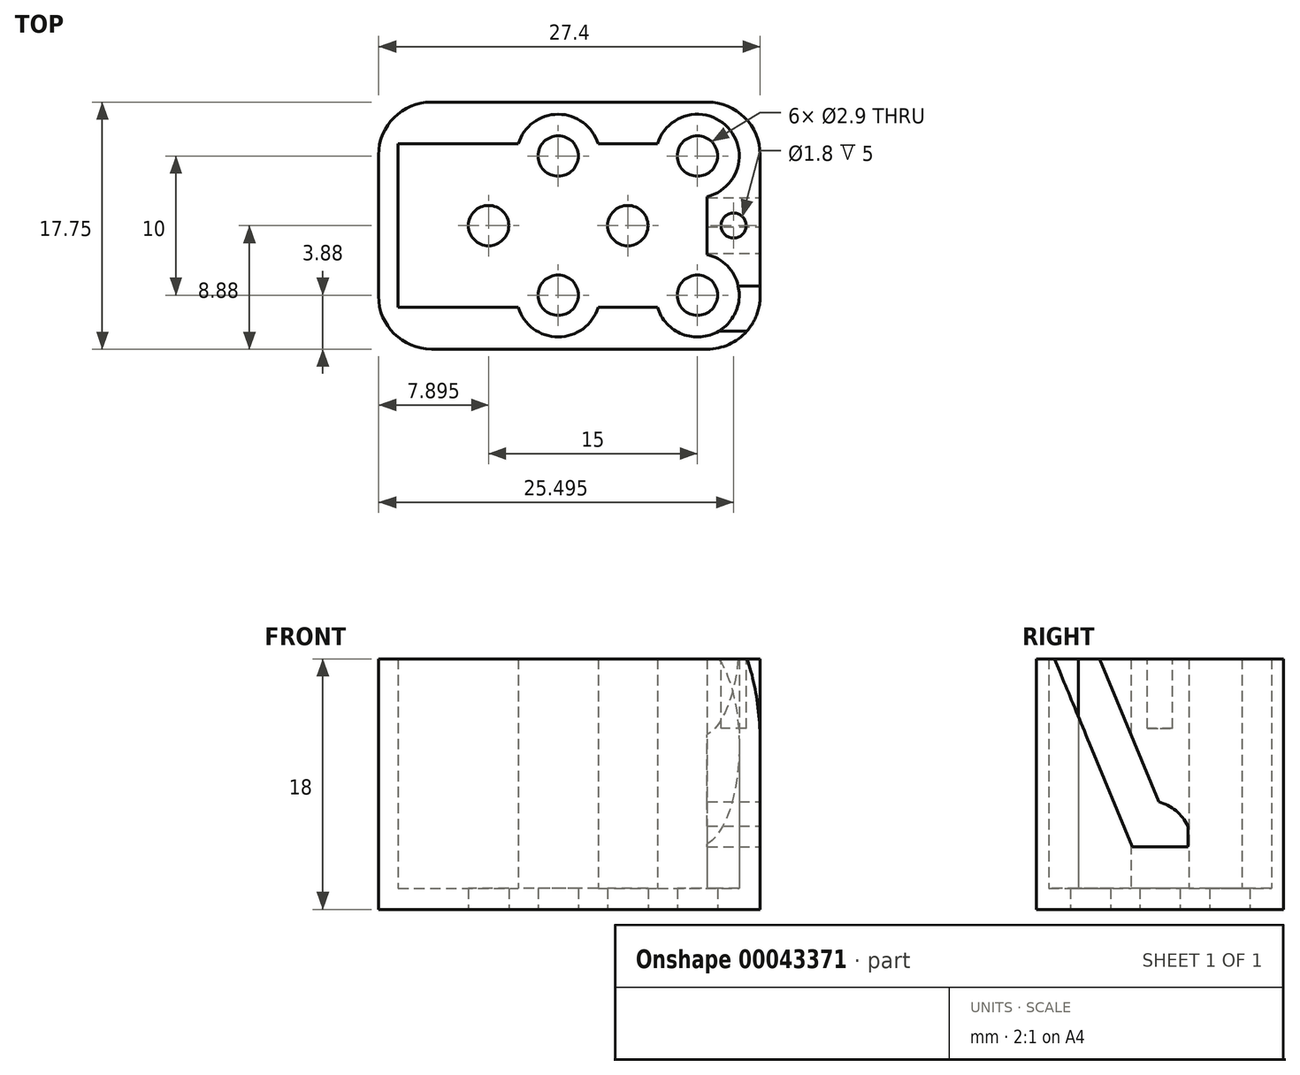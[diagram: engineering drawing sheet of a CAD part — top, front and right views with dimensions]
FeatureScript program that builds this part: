
annotation { "Feature Type Name" : "Feature", "Feature Type Description" : "" }
export const myFeature = defineFeature(function(context is Context, id is Id, definition is map)
    precondition{}
    {
        {
            var Q0;
            Q0=qCreatedBy(makeId("Top.planeOp"),FACE);
            var sketch = newSketch(context, id + "F0", { "sketchPlane" : qUnion([Q0])});
            skLineSegment(sketch, "E0.bottom", {"start": v(-11.23, 5.28) * mm, "end": v(10.27, 5.28) * mm});
            skLineSegment(sketch, "E0.top", {"start": v(-11.23, -6.47) * mm, "end": v(10.27, -6.47) * mm});
            skLineSegment(sketch, "E0.left", {"start": v(-11.23, 5.28) * mm, "end": v(-11.23, -6.47) * mm});
            skLineSegment(sketch, "E0.right", {"start": v(10.27, 5.28) * mm, "end": v(10.27, -6.47) * mm});
            skPoint(sketch, "E1", {"position": v(-0.48, -0.6) * mm});
            skPoint(sketch, "E1.positionSnap0", {"position": v(10.27, -0.6) * mm});
            skPoint(sketch, "E1.positionSnap1", {"position": v(-0.48, 5.28) * mm});
            skLineSegment(sketch, "E2.bottom", {"start": v(-12.63, 8.28) * mm, "end": v(11.67, 8.28) * mm});
            skLineSegment(sketch, "E2.left", {"start": v(-12.63, 8.28) * mm, "end": v(-12.63, -9.47) * mm});
            skPoint(sketch, "E3", {"position": v(-0.48, 8.28) * mm});
            skLineSegment(sketch, "E4.bottom", {"start": v(11.67, 8.28) * mm, "end": v(14.77, 8.28) * mm});
            skLineSegment(sketch, "E4.top", {"start": v(-12.63, -9.47) * mm, "end": v(14.77, -9.47) * mm});
            skLineSegment(sketch, "E4.right", {"start": v(14.77, 8.28) * mm, "end": v(14.77, -9.47) * mm});
            skPoint(sketch, "E5", {"position": v(5.27, -0.6) * mm});
            skCircle(sketch, "E6", {"center": v(5.27, -0.6) * mm, "radius": 1.45 * mm});
            skLineSegment(sketch, "E7.bottom", {"start": v(0.27, 4.4) * mm, "end": v(5.27, 4.4) * mm, "construction": true});
            skLineSegment(sketch, "E7.top", {"start": v(0.27, -5.6) * mm, "end": v(10.27, -5.6) * mm, "construction": true});
            skLineSegment(sketch, "E7.left", {"start": v(0.27, 4.4) * mm, "end": v(0.27, -5.6) * mm, "construction": true});
            skLineSegment(sketch, "E7.right", {"start": v(10.27, 4.4) * mm, "end": v(10.27, -5.6) * mm, "construction": true});
            skPoint(sketch, "E8.positionSnap1", {"position": v(5.27, 4.4) * mm});
            skCircle(sketch, "E9", {"center": v(10.27, 4.4) * mm, "radius": 1.45 * mm});
            skCircle(sketch, "E10.0.1.0", {"center": v(10.27, -5.6) * mm, "radius": 1.45 * mm});
            skCircle(sketch, "E10.1.0.0", {"center": v(0.27, 4.4) * mm, "radius": 1.45 * mm});
            skCircle(sketch, "E10.1.1.0", {"center": v(0.27, -5.6) * mm, "radius": 1.45 * mm});
            skLineSegment(sketch, "E10.direction1", {"start": v(10.27, 4.4) * mm, "end": v(7.27, 4.4) * mm, "construction": true});
            skCircle(sketch, "E11.1.0.0", {"center": v(-4.73, -0.6) * mm, "radius": 1.45 * mm});
            skLineSegment(sketch, "E11.direction1", {"start": v(5.27, -0.6) * mm, "end": v(-4.73, -0.6) * mm, "construction": true});
            skCircle(sketch, "E12", {"center": v(10.27, 4.4) * mm, "radius": 3 * mm});
            skCircle(sketch, "E13.0.1.0", {"center": v(10.27, -5.6) * mm, "radius": 3 * mm});
            skCircle(sketch, "E13.1.0.0", {"center": v(0.27, 4.4) * mm, "radius": 3 * mm});
            skCircle(sketch, "E13.1.1.0", {"center": v(0.27, -5.6) * mm, "radius": 3 * mm});
            skLineSegment(sketch, "E13.direction1", {"start": v(10.27, 4.4) * mm, "end": v(0.27, 4.4) * mm, "construction": true});
            skLineSegment(sketch, "E14.trimOffspring", {"start": v(3.27, 4.4) * mm, "end": v(0.27, 4.4) * mm, "construction": true});
            skLineSegment(sketch, "E15.trimOffspring", {"start": v(7.27, 4.4) * mm, "end": v(10.27, 4.4) * mm, "construction": true});
            skLineSegment(sketch, "E16", {"start": v(10.97, 1.5) * mm, "end": v(10.97, -2.67) * mm});
            skSolve(sketch);
        }
        {
            var Q0;
            {var subQ6=sQuery(id+"F0.wireOp",EDGE,"E0.left");Q0=makeQuery(id+"F0.imprint","IMPRINT",FACE,{"disambiguationData":[TD([[makeQuery(id+"F0.imprint","IMPRINT",EDGE,{"derivedFrom":subQ6}),1.0]])]});}
            var Q1;
            {var subQ0=sQuery(id+"F0.wireOp",EDGE,"E13.0.1.0");var subQ3=sQuery(id+"F0.wireOp",EDGE,"E0.top");var subQ4=makeQuery(id+"F0.imprint","INTERSECT",VERTEX,{"derivedFrom":[subQ3,subQ0]});Q1=makeQuery(id+"F0.imprint","IMPRINT",FACE,{"disambiguationData":[TD([[makeQuery(id+"F0.imprint","IMPRINT",EDGE,{"disambiguationData":[TD([[subQ4,-1.0]])],"derivedFrom":subQ3}),1.0]])]});}
            var Q2;
            {var subQ3=sQuery(id+"F0.wireOp",EDGE,"E0.bottom");var subQ5=sQuery(id+"F0.wireOp",EDGE,"E12");var subQ7=makeQuery(id+"F0.imprint","INTERSECT",VERTEX,{"derivedFrom":[subQ3,subQ5]});Q2=makeQuery(id+"F0.imprint","IMPRINT",FACE,{"disambiguationData":[TD([[makeQuery(id+"F0.imprint","IMPRINT",EDGE,{"disambiguationData":[TD([[subQ7,-1.0]])],"derivedFrom":subQ3}),-1.0]])]});}
            var Q3;
            {var subQ0=sQuery(id+"F0.wireOp",EDGE,"E13.0.1.0");var subQ3=sQuery(id+"F0.wireOp",EDGE,"E0.top");var subQ4=makeQuery(id+"F0.imprint","INTERSECT",VERTEX,{"derivedFrom":[subQ3,subQ0]});Q3=makeQuery(id+"F0.imprint","IMPRINT",FACE,{"disambiguationData":[TD([[makeQuery(id+"F0.imprint","IMPRINT",EDGE,{"disambiguationData":[TD([[subQ4,-1.0]])],"derivedFrom":subQ3}),-1.0]])]});}
            var Q4;
            {var subQ1=sQuery(id+"F0.wireOp",EDGE,"E0.bottom");var subQ4=sQuery(id+"F0.wireOp",EDGE,"E13.1.0.0");var subQ6=makeQuery(id+"F0.imprint","INTERSECT",VERTEX,{"disambiguationData":[OD(0.0)],"derivedFrom":[subQ1,subQ4]});Q4=makeQuery(id+"F0.imprint","IMPRINT",FACE,{"disambiguationData":[TD([[makeQuery(id+"F0.imprint","IMPRINT",EDGE,{"disambiguationData":[TD([[subQ6,-1.0]])],"derivedFrom":subQ1}),1.0]])]});}
            var Q5;
            {var subQ0=sQuery(id+"F0.wireOp",EDGE,"E13.1.0.0");var subQ1=sQuery(id+"F0.wireOp",EDGE,"E0.bottom");var subQ3=makeQuery(id+"F0.imprint","INTERSECT",VERTEX,{"disambiguationData":[OD(0.0)],"derivedFrom":[subQ1,subQ0]});Q5=makeQuery(id+"F0.imprint","IMPRINT",FACE,{"disambiguationData":[TD([[makeQuery(id+"F0.imprint","IMPRINT",EDGE,{"disambiguationData":[TD([[subQ3,-1.0]])],"derivedFrom":subQ1}),-1.0]])]});}
            var Q6;
            {var subQ3=sQuery(id+"F0.wireOp",EDGE,"E0.bottom");var subQ5=sQuery(id+"F0.wireOp",EDGE,"E12");var subQ7=makeQuery(id+"F0.imprint","INTERSECT",VERTEX,{"derivedFrom":[subQ3,subQ5]});Q6=makeQuery(id+"F0.imprint","IMPRINT",FACE,{"disambiguationData":[TD([[makeQuery(id+"F0.imprint","IMPRINT",EDGE,{"disambiguationData":[TD([[subQ7,-1.0]])],"derivedFrom":subQ3}),1.0]])]});}
            var Q7;
            {var subQ0=sQuery(id+"F0.wireOp",EDGE,"E13.1.1.0");var subQ1=sQuery(id+"F0.wireOp",EDGE,"E0.top");var subQ3=makeQuery(id+"F0.imprint","INTERSECT",VERTEX,{"disambiguationData":[OD(0.0)],"derivedFrom":[subQ1,subQ0]});Q7=makeQuery(id+"F0.imprint","IMPRINT",FACE,{"disambiguationData":[TD([[makeQuery(id+"F0.imprint","IMPRINT",EDGE,{"disambiguationData":[TD([[subQ3,-1.0]])],"derivedFrom":subQ1}),1.0]])]});}
            var Q8;
            {var subQ1=sQuery(id+"F0.wireOp",EDGE,"E0.top");var subQ4=sQuery(id+"F0.wireOp",EDGE,"E13.1.1.0");var subQ6=makeQuery(id+"F0.imprint","INTERSECT",VERTEX,{"disambiguationData":[OD(0.0)],"derivedFrom":[subQ1,subQ4]});Q8=makeQuery(id+"F0.imprint","IMPRINT",FACE,{"disambiguationData":[TD([[makeQuery(id+"F0.imprint","IMPRINT",EDGE,{"disambiguationData":[TD([[subQ6,-1.0]])],"derivedFrom":subQ1}),-1.0]])]});}
            var Q9;
            {var subQ0=sQuery(id+"F0.wireOp",EDGE,"E16");Q9=makeQuery(id+"F0.imprint","IMPRINT",FACE,{"disambiguationData":[TD([[makeQuery(id+"F0.imprint","IMPRINT",EDGE,{"derivedFrom":subQ0}),-1.0]])]});}
            extrude(context, id + "F1", {"entities" : qUnion([Q0, Q1, Q2, Q3, Q4, Q5, Q6, Q7, Q8, Q9]), "depth" : 1.5 * mm});
        }
        {
            var Q0;
            {var subQ15=sQuery(id+"F0.wireOp",EDGE,"E0.left");Q0=makeQuery(id+"F0.imprint","IMPRINT",FACE,{"disambiguationData":[TD([[makeQuery(id+"F0.imprint","IMPRINT",EDGE,{"derivedFrom":subQ15}),-1.0]])]});}
            extrude(context, id + "F2", {"entities" : qUnion([Q0]), "operationType" : NewBodyOperationType.ADD, "depth" : 18 * mm});
        }
        {
            var Q0;
            Q0=makeQuery(id+"F2.opExtrude","CAP_FACE",FACE,{"disambiguationData":[OSD([sQuery(id+"F0.wireOp",EDGE,"E0.bottom"),sQuery(id+"F0.wireOp",EDGE,"E0.top"),sQuery(id+"F0.wireOp",EDGE,"E0.left"),sQuery(id+"F0.wireOp",EDGE,"E0.right"),sQuery(id+"F0.wireOp",EDGE,"E2.bottom"),sQuery(id+"F0.wireOp",EDGE,"E2.left"),sQuery(id+"F0.wireOp",EDGE,"E4.bottom"),sQuery(id+"F0.wireOp",EDGE,"E4.top"),sQuery(id+"F0.wireOp",EDGE,"E4.right"),sQuery(id+"F0.wireOp",EDGE,"E12"),sQuery(id+"F0.wireOp",EDGE,"E13.0.1.0"),sQuery(id+"F0.wireOp",EDGE,"E13.1.0.0"),sQuery(id+"F0.wireOp",EDGE,"E13.1.1.0")])],"isStart":false});
            var sketch = newSketch(context, id + "F3", { "sketchPlane" : qUnion([Q0])});
            skLineSegment(sketch, "E17", {"start": v(10.97, 1.5) * mm, "end": v(10.97, -2.67) * mm, "construction": true});
            skLineSegment(sketch, "E18", {"start": v(14.77, 8.28) * mm, "end": v(14.77, -9.47) * mm, "construction": true});
            skLineSegment(sketch, "E19", {"start": v(10.97, -0.6) * mm, "end": v(14.77, -0.6) * mm, "construction": true});
            skCircle(sketch, "E20", {"center": v(12.87, -0.6) * mm, "radius": 0.9 * mm});
            skSolve(sketch);
        }
        {
            var Q0;
            Q0 = qSketchRegion(id + "F3", true);
            var Q1;
            Q1=makeQuery(id+"F3.imprint","IMPRINT",FACE,{"disambiguationData":[TD([[makeQuery(id+"F3.imprint","IMPRINT",EDGE,{"derivedFrom":sQuery(id+"F3.wireOp",EDGE,"E20")}),1.0]])]});
            extrude(context, id + "F4", {"entities" : qUnion([Q0, Q1]), "operationType" : NewBodyOperationType.REMOVE, "oppositeDirection" : true, "depth" : 5 * mm});
        }
        {
            var Q0;
            Q0=makeQuery(id+"F2.opExtrude","SWEPT_FACE",FACE,{"disambiguationData":[OSD([sQuery(id+"F0.wireOp",EDGE,"E4.right")])]});
            var sketch = newSketch(context, id + "F5", { "sketchPlane" : qUnion([Q0])});
            skLineSegment(sketch, "E21.bottom", {"start": v(-9.47, 18) * mm, "end": v(8.28, 18) * mm, "construction": true});
            skLineSegment(sketch, "E21.top", {"start": v(-9.47, 0) * mm, "end": v(8.28, 0) * mm, "construction": true});
            skLineSegment(sketch, "E21.left", {"start": v(-9.47, 18) * mm, "end": v(-9.47, 0) * mm, "construction": true});
            skLineSegment(sketch, "E21.right", {"start": v(8.28, 18) * mm, "end": v(8.28, 0) * mm, "construction": true});
            skPoint(sketch, "E22", {"position": v(-0.6, 0) * mm});
            skLineSegment(sketch, "E23.bottom", {"start": v(-2.6, 6) * mm, "end": v(1.4, 6) * mm});
            skLineSegment(sketch, "E23.top", {"start": v(-2.6, 4.5) * mm, "end": v(1.4, 4.5) * mm});
            skLineSegment(sketch, "E23.left", {"start": v(-2.6, 6) * mm, "end": v(-2.6, 4.5) * mm});
            skLineSegment(sketch, "E23.right", {"start": v(1.4, 6) * mm, "end": v(1.4, 4.5) * mm});
            skPoint(sketch, "E24", {"position": v(-0.6, 4.5) * mm});
            skLineSegment(sketch, "E25", {"start": v(-2.6, 4.5) * mm, "end": v(-8.17, 18) * mm});
            skLineSegment(sketch, "E26", {"start": v(0.04, 6) * mm, "end": v(-4.92, 18) * mm});
            skLineSegment(sketch, "E27", {"start": v(-8.17, 18) * mm, "end": v(-4.92, 18) * mm});
            skArc(sketch, "E28", {"start": v(1.4, 6) * mm, "mid": v(0.55, 7.09) * mm, "end": v(-0.68, 7.73) * mm});
            skSolve(sketch);
        }
        {
            var Q0;
            Q0=makeQuery(id+"F5.imprint","IMPRINT",FACE,{"disambiguationData":[TD([[makeQuery(id+"F5.imprint","IMPRINT",EDGE,{"derivedFrom":sQuery(id+"F5.wireOp",EDGE,"E23.left")}),-1.0]])]});
            var Q1;
            Q1=makeQuery(id+"F5.imprint","IMPRINT",FACE,{"disambiguationData":[TD([[makeQuery(id+"F5.imprint","IMPRINT",EDGE,{"derivedFrom":sQuery(id+"F5.wireOp",EDGE,"E23.bottom")}),-1.0]])]});
            var Q2;
            Q2=makeQuery(id+"F5.imprint","IMPRINT",FACE,{"disambiguationData":[TD([[makeQuery(id+"F5.imprint","IMPRINT",EDGE,{"derivedFrom":sQuery(id+"F5.wireOp",EDGE,"E23.bottom")}),1.0]])]});
            extrude(context, id + "F6", {"entities" : qUnion([Q0, Q1, Q2]), "operationType" : NewBodyOperationType.REMOVE, "oppositeDirection" : true, "depth" : 5 * mm});
        }
        {
            var Q0;
            Q0=makeQuery(id+"F2.opExtrude","SWEPT_EDGE",EDGE,{"disambiguationData":[OSD([sQuery(id+"F0.wireOp",EDGE,"E4.bottom"),sQuery(id+"F0.wireOp",EDGE,"E4.right")])]});
            var Q1;
            Q1=makeQuery(id+"F2.opExtrude","SWEPT_EDGE",EDGE,{"disambiguationData":[OSD([sQuery(id+"F0.wireOp",EDGE,"E2.bottom"),sQuery(id+"F0.wireOp",EDGE,"E2.left")])]});
            var Q2;
            Q2=makeQuery(id+"F2.opExtrude","SWEPT_EDGE",EDGE,{"disambiguationData":[OSD([sQuery(id+"F0.wireOp",EDGE,"E2.left"),sQuery(id+"F0.wireOp",EDGE,"E4.top")])]});
            var Q3;
            Q3=makeQuery(id+"F2.opExtrude","SWEPT_EDGE",EDGE,{"disambiguationData":[OSD([sQuery(id+"F0.wireOp",EDGE,"E4.top"),sQuery(id+"F0.wireOp",EDGE,"E4.right")])]});
            fillet(context, id + "F7", {"entities" : qUnion([Q0, Q1, Q2, Q3]), "radius" : 3.8 * mm, "tangentPropagation" : true, "allowEdgeOverflow" : false});
        }
    });
